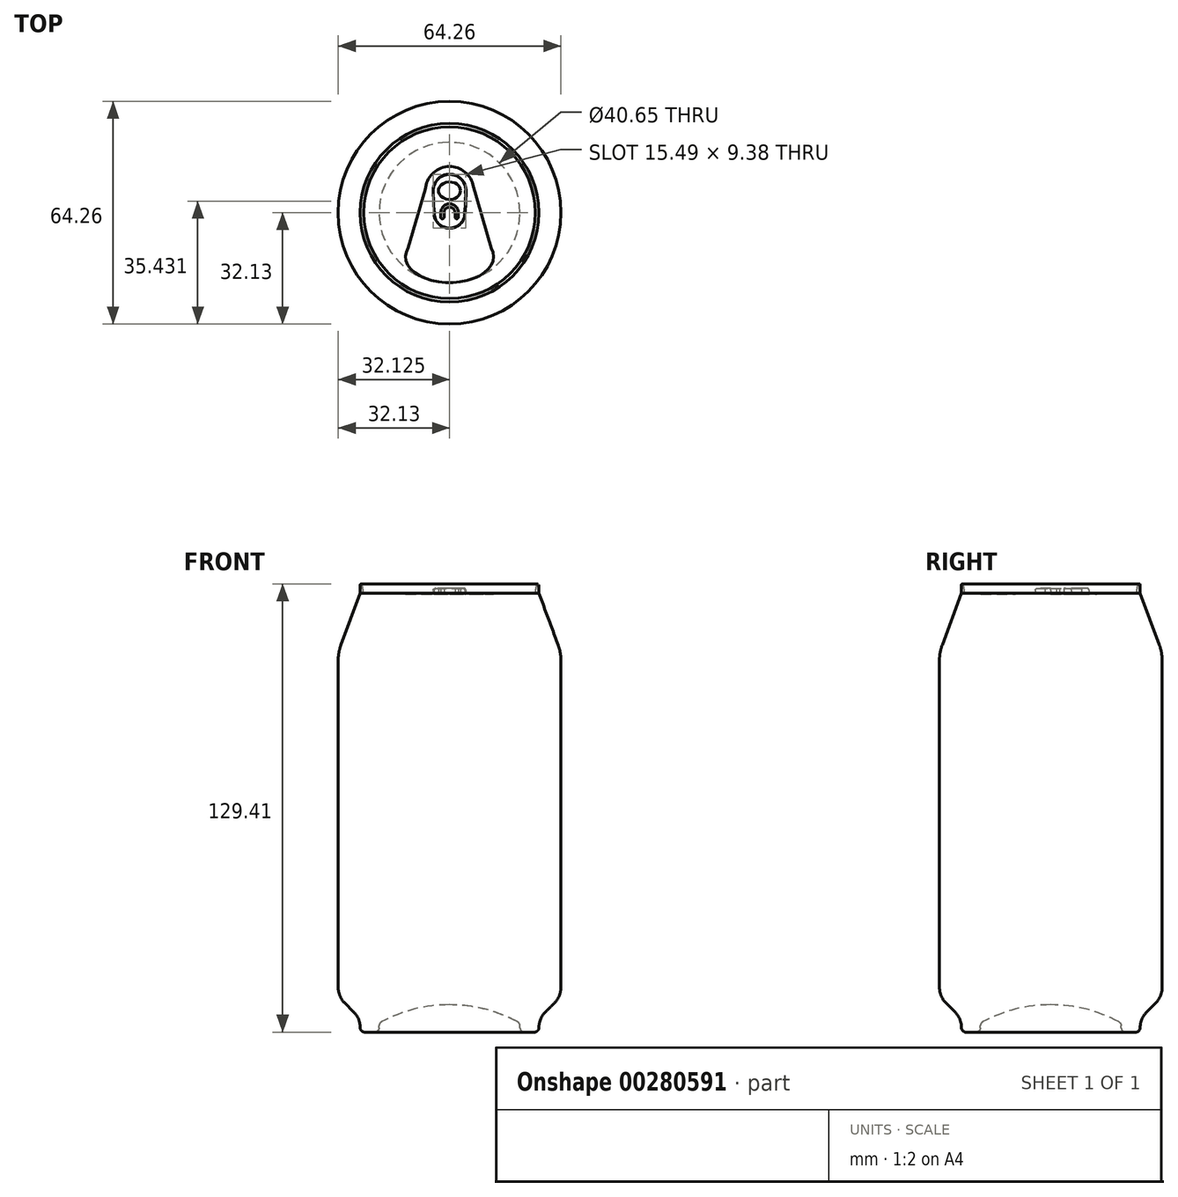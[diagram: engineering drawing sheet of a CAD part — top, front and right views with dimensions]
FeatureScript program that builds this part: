
annotation { "Feature Type Name" : "Feature", "Feature Type Description" : "" }
export const myFeature = defineFeature(function(context is Context, id is Id, definition is map)
    precondition{}
    {
        {
            var Q0;
            Q0=qCreatedBy(makeId("Front.planeOp"),FACE);
            var sketch = newSketch(context, id + "F0", { "sketchPlane" : qUnion([Q0])});
            skLineSegment(sketch, "E0", {"start": v(21.6, -34.59) * mm, "end": v(24.51, -34.59) * mm});
            skLineSegment(sketch, "E1", {"start": v(32.13, -21.68) * mm, "end": v(32.13, 72.73) * mm});
            skLineSegment(sketch, "E2", {"start": v(24.76, 92.15) * mm, "end": v(0, 92.15) * mm});
            skLineSegment(sketch, "E3", {"start": v(25.78, -33.32) * mm, "end": v(25.78, -33.3) * mm});
            skLineSegment(sketch, "E4", {"start": v(27.64, -28.8) * mm, "end": v(30.27, -26.17) * mm});
            skPoint(sketch, "E5.orphan", {"position": v(32.13, -34.59) * mm});
            skLineSegment(sketch, "E6", {"start": v(20.33, -33.32) * mm, "end": v(20.33, -32.77) * mm});
            skArc(sketch, "E7", {"start": v(0, -26.7) * mm, "mid": v(10.14, -27.95) * mm, "end": v(19.66, -31.65) * mm});
            skPoint(sketch, "E8.orphan", {"position": v(0, -34.59) * mm});
            skPoint(sketch, "E9.visualSharp", {"position": v(20.33, -34.59) * mm});
            skArc(sketch, "E9.filletArc", {"start": v(20.33, -33.32) * mm, "mid": v(20.7, -34.22) * mm, "end": v(21.6, -34.59) * mm});
            skPoint(sketch, "E10.visualSharp", {"position": v(25.78, -34.59) * mm});
            skArc(sketch, "E10.filletArc", {"start": v(24.51, -34.59) * mm, "mid": v(25.4, -34.22) * mm, "end": v(25.78, -33.32) * mm});
            skPoint(sketch, "E11.visualSharp", {"position": v(20.33, -32.02) * mm});
            skArc(sketch, "E11.filletArc", {"start": v(20.33, -32.77) * mm, "mid": v(20.15, -32.12) * mm, "end": v(19.66, -31.65) * mm});
            skPoint(sketch, "E12.visualSharp", {"position": v(25.78, -30.66) * mm});
            skArc(sketch, "E12.filletArc", {"start": v(27.64, -28.8) * mm, "mid": v(26.26, -30.86) * mm, "end": v(25.78, -33.3) * mm});
            skPoint(sketch, "E13.visualSharp", {"position": v(32.13, -24.31) * mm});
            skArc(sketch, "E13.filletArc", {"start": v(30.27, -26.17) * mm, "mid": v(31.65, -24.11) * mm, "end": v(32.13, -21.68) * mm});
            skLineSegment(sketch, "E14", {"start": v(25.78, 92.15) * mm, "end": v(31.34, 77.14) * mm});
            skPoint(sketch, "E15.orphan", {"position": v(32.13, 92.15) * mm});
            skPoint(sketch, "E16.visualSharp", {"position": v(32.13, 75) * mm});
            skArc(sketch, "E16.filletArc", {"start": v(32.13, 72.73) * mm, "mid": v(31.93, 74.97) * mm, "end": v(31.34, 77.14) * mm});
            skLineSegment(sketch, "E17", {"start": v(25.78, 92.15) * mm, "end": v(25.78, 94.5) * mm});
            skLineSegment(sketch, "E18", {"start": v(25.15, 94.55) * mm, "end": v(24.76, 92.15) * mm});
            skPoint(sketch, "E19.visualSharp", {"position": v(25.78, 98.5) * mm});
            skArc(sketch, "E19.filletArc", {"start": v(25.78, 94.5) * mm, "mid": v(25.49, 94.82) * mm, "end": v(25.15, 94.55) * mm});
            skLineSegment(sketch, "E20", {"start": v(0, 92.15) * mm, "end": v(0, -26.7) * mm});
            skSolve(sketch);
        }
        {
            var Q0;
            Q0=qCreatedBy(makeId("Front.planeOp"),FACE);
            var sketch = newSketch(context, id + "F1", { "sketchPlane" : qUnion([Q0])});
            skLineSegment(sketch, "E21", {"start": v(0, 93.47) * mm, "end": v(0, -27.53) * mm});
            skSolve(sketch);
        }
        {
            var Q0;
            Q0 = qSketchRegion(id + "F0", true);
            var Q1;
            Q1=sQuery(id+"F1.wireOp",EDGE,"E21");
            revolve(context, id + "F2", {"entities" : qUnion([Q0]), "axis" : qUnion([Q1]), "revolveType" : RevolveType.FULL});
        }
        {
            var Q0;
            Q0=makeQuery(id+"F2.opRevolve","SWEPT_FACE",FACE,{"disambiguationData":[OSD([sQuery(id+"F0.wireOp",EDGE,"E2")])]});
            var sketch = newSketch(context, id + "F3", { "sketchPlane" : qUnion([Q0])});
            skArc(sketch, "E22", {"start": v(6.97, 6.35) * mm, "mid": v(0.23, 13.32) * mm, "end": v(-6.96, 6.8) * mm});
            skPoint(sketch, "E23.orphan", {"position": v(6.97, 6.35) * mm});
            skPoint(sketch, "E24.center.orphan", {"position": v(0, -12.7) * mm});
            skEllipticalArc(sketch, "E25", {});
            skLineSegment(sketch, "E26", {"start": v(6.67, 8.39) * mm, "end": v(12.7, -12.7) * mm});
            skLineSegment(sketch, "E27", {"start": v(-6.96, 6.8) * mm, "end": v(-12.7, -12.7) * mm});
            const initialGuessF3  = {"E25": [0, -0.0127, 1, 0, 0.012695110403001308, 0.007481287579920419, 2.7982343358633526, 0.33376044429198093]};
            skSetInitialGuess(sketch, initialGuessF3);
            skSolve(sketch);
        }
        {
            var Q0;
            Q0 = qSketchRegion(id + "F3", true);
            extrude(context, id + "F4", {"entities" : qUnion([Q0]), "operationType" : NewBodyOperationType.REMOVE, "oppositeDirection" : true, "depth" : 0.25 * mm});
        }
        {
            var Q0;
            Q0=makeQuery(id+"F4.boolean.opBoolean","COPY",FACE,{"derivedFrom":makeQuery(id+"F4.opExtrude","CAP_FACE",FACE,{"disambiguationData":[OSD([sQuery(id+"F3.wireOp",EDGE,"E22"),sQuery(id+"F3.wireOp",EDGE,"E25"),sQuery(id+"F3.wireOp",EDGE,"E26"),sQuery(id+"F3.wireOp",EDGE,"E27")])],"isStart":false})});
            var sketch = newSketch(context, id + "F5", { "sketchPlane" : qUnion([Q0])});
            skArc(sketch, "E28", {"start": v(4.68, 5.97) * mm, "mid": v(0.1, 11.05) * mm, "end": v(-4.7, 6.16) * mm});
            skArc(sketch, "E29", {"start": v(-4.45, 0) * mm, "mid": v(0, -4.45) * mm, "end": v(4.45, 0) * mm});
            skLineSegment(sketch, "E30", {"start": v(4.44, 0) * mm, "end": v(4.7, 6.35) * mm});
            skLineSegment(sketch, "E31", {"start": v(-4.44, 0) * mm, "end": v(-4.7, 6.35) * mm});
            skArc(sketch, "E32", {"start": v(2.54, 0) * mm, "mid": v(0, 2.54) * mm, "end": v(-2.54, 0) * mm});
            skArc(sketch, "E33", {"start": v(1.59, 0) * mm, "mid": v(0, 1.59) * mm, "end": v(-1.59, 0) * mm});
            skLineSegment(sketch, "E34", {"start": v(1.59, 0) * mm, "end": v(1.59, -1.27) * mm});
            skLineSegment(sketch, "E35", {"start": v(2.54, 0) * mm, "end": v(2.54, -1.27) * mm});
            skLineSegment(sketch, "E36", {"start": v(-1.59, 0) * mm, "end": v(-1.59, -1.27) * mm});
            skLineSegment(sketch, "E37", {"start": v(-2.54, 0) * mm, "end": v(-2.54, -1.27) * mm});
            skArc(sketch, "E38", {"start": v(1.59, -1.27) * mm, "mid": v(2.06, -1.75) * mm, "end": v(2.54, -1.27) * mm});
            skArc(sketch, "E39", {"start": v(-1.59, -1.27) * mm, "mid": v(-2.06, -1.75) * mm, "end": v(-2.54, -1.27) * mm});
            skEllipse(sketch, "E40", {"center": v(0, 6.35) * mm, "majorRadius": 3.18 * mm, "minorRadius": 2.54 * mm, "majorAxis": v(1, 0)});
            skSolve(sketch);
        }
        {
            var Q0;
            Q0 = qSketchRegion(id + "F5", true);
            extrude(context, id + "F6", {"entities" : qUnion([Q0]), "operationType" : NewBodyOperationType.ADD, "depth" : 1.59 * mm});
        }
        {
            var Q0;
            Q0=makeQuery(id+"F6.opExtrude","CAP_EDGE",EDGE,{"disambiguationData":[OSD([sQuery(id+"F5.wireOp",EDGE,"E31")])],"isStart":false});
            var Q1;
            Q1=makeQuery(id+"F6.opExtrude","CAP_EDGE",EDGE,{"disambiguationData":[OSD([sQuery(id+"F5.wireOp",EDGE,"E28")])],"isStart":false});
            var Q2;
            Q2=makeQuery(id+"F6.opExtrude","CAP_EDGE",EDGE,{"disambiguationData":[OSD([sQuery(id+"F5.wireOp",EDGE,"E29")])],"isStart":false});
            var Q3;
            Q3=makeQuery(id+"F6.opExtrude","CAP_EDGE",EDGE,{"disambiguationData":[OSD([sQuery(id+"F5.wireOp",EDGE,"E29")])],"isStart":true});
            var Q4;
            Q4=makeQuery(id+"F6.opExtrude","CAP_EDGE",EDGE,{"disambiguationData":[OSD([sQuery(id+"F5.wireOp",EDGE,"E31")])],"isStart":true});
            var Q5;
            Q5=makeQuery(id+"F6.opExtrude","CAP_EDGE",EDGE,{"disambiguationData":[OSD([sQuery(id+"F5.wireOp",EDGE,"E28")])],"isStart":true});
            var Q6;
            Q6=makeQuery(id+"F6.opExtrude","CAP_EDGE",EDGE,{"disambiguationData":[OSD([sQuery(id+"F5.wireOp",EDGE,"E30")])],"isStart":false});
            var Q7;
            Q7=makeQuery(id+"F6.opExtrude","CAP_EDGE",EDGE,{"disambiguationData":[OSD([sQuery(id+"F5.wireOp",EDGE,"E30")])],"isStart":true});
            fillet(context, id + "F7", {"entities" : qUnion([Q0, Q1, Q2, Q3, Q4, Q5, Q6, Q7]), "radius" : 0.5 * mm, "tangentPropagation" : true, "allowEdgeOverflow" : false});
        }
    });
